# Revit family: Grohe_FlushPlate_Skate_38505KF0
name_source: partatom
category: Plumbing Fixtures
units: mm (PartAtom-declared; Revit-internal decimal feet)

## family parameters
Cut with Voids When Loaded = No
Host = Face
OmniClass Number = 23.45.05.00
OmniClass Title = Sanitary Equipment
Part Type = Normal
Room Calculation Point = No
Round Connector Dimension = Use Diameter
Shared = No

## types (1)
- SKATE Flush Plate (38505KF0)
    Assembly Code = D2010
    AssetType = Fixed
    BIMObjectName = Grohe_FlushPlate_Skate_38505KF0
    CO2NeutralProduction = GROHE is one of the first leading manufacturer within the sanitary industry having a CO2-neutral production.
    CW Connection = No
    ClassificationName = Uniclass2015
    ClassificationValue = Pr_75_50_46_68
    Color = Matt Black
    Cost = 0 $
    Default Elevation = 0 mm  [stored 0 ft]
    Description = SKATE Flush Plate
    DimensionsDocumentLink = https://cdn.cloud.grohe.com
    DocumentationCertificates = https://www.bimstore.co
    DocumentationInstallationGuide = https://www.bimstore.co
    DocumentationLiterature = https://www.bimstore.co
    DocumentationMaintenance = https://www.bimstore.co
    DocumentationTechnical = https://www.bimstore.co
    DurationUnit = Years
    EF000007 = Black
    EF000008 = 156 mm  [stored 0.511811 ft]
    EF000040 = 11 mm  [stored 0.0360892 ft]
    EF001438 = 197 mm
    EF002147 = Two button
    EF002169 = Plastic
    EF006331 = FALSE
    EF006949 = Pneumatic
    EF010109 = FALSE
    EF020827 = TRUE
    EF020828 = TRUE
    EF023751 = TRUE
    EF023752 = TRUE
    Ecojoy = No
    ExpectedLife = 0
    FullRecyclabilityOfPlastic = All plastic components are fully recyclable
    GROHESocialCommittment = green.grohe.com/social_engagement
    GROHESustainability = green.grohe.com
    HW Connection = No
    IfcExportAs = IfcPipeFitting
    IfcExportType = IfcPipeFittingType
    Keynote = N13
    Manufacturer = Grohe
    ManufacturerName = Grohe
    Model = SKATE Flush Plate
    ModelNumber = 38505KF0
    ModelReference = SKATE Flush Plate
    NBSDescription = Push-button flush controllers
    NBSObjectName = Grohe - Push-button flush controllers
    NominalDepth = 0 mm  [stored 0 ft]
    NominalHeight = 0 mm  [stored 0 ft]
    NominalLength = 0 mm  [stored 0 ft]
    PrimaryMaterial = Grohe_MattBlack
    ProductDescription = for dual flush or start & stop actuation

for pneumatic discharge valve

vertical installation

156 x 197 mm

made of ABS

GROHE Long-Life Shine finish

GROHE Water Saving - Less water, perfect flow

for combination with Rapid SL and Uniset with GD 2 cistern

for use with Rapid SLX please order shaft 66 791 000 (sold separately)
    ProductNumber = 38505KF0
    ProductPageURL = https://www.grohe.co.uk
    ProductShortText = Skate Air Flush Plate
    ProductType = Manual Actuation
    ProductionYear = 2023
    SustainabilityAward = green.grohe.com/awards
    SustainabilityReport = green.grohe.com/reporting
    TPIDocumentLink = https://cdn.cloud.grohe.com
    Type Comments = SKATE Flush Plate
    TypeName = SKATE Flush Plate
    URL = https://www.grohe.co.uk
    Vent Connection = No
    WarrantyDurationLabor = 0
    WarrantyDurationParts = 0
    WarrantyDurationUnit = Years
    Waste Connection = No
    _BSBibleVersion = 17
    _BimSpecGuid = 0
    _CurrentRevision = 1
    _DistributedBy = https://www.bimstore.co
    _ObjectUserGuide = https://www.bimstore.co

note: [stored X ft] marks values corroborated as IEEE doubles in the binary element streams (Revit-internal decimal feet)

## geometry (parser evidence)
native form markers: Sweep x2
no freeform markers — native parametric forms only
